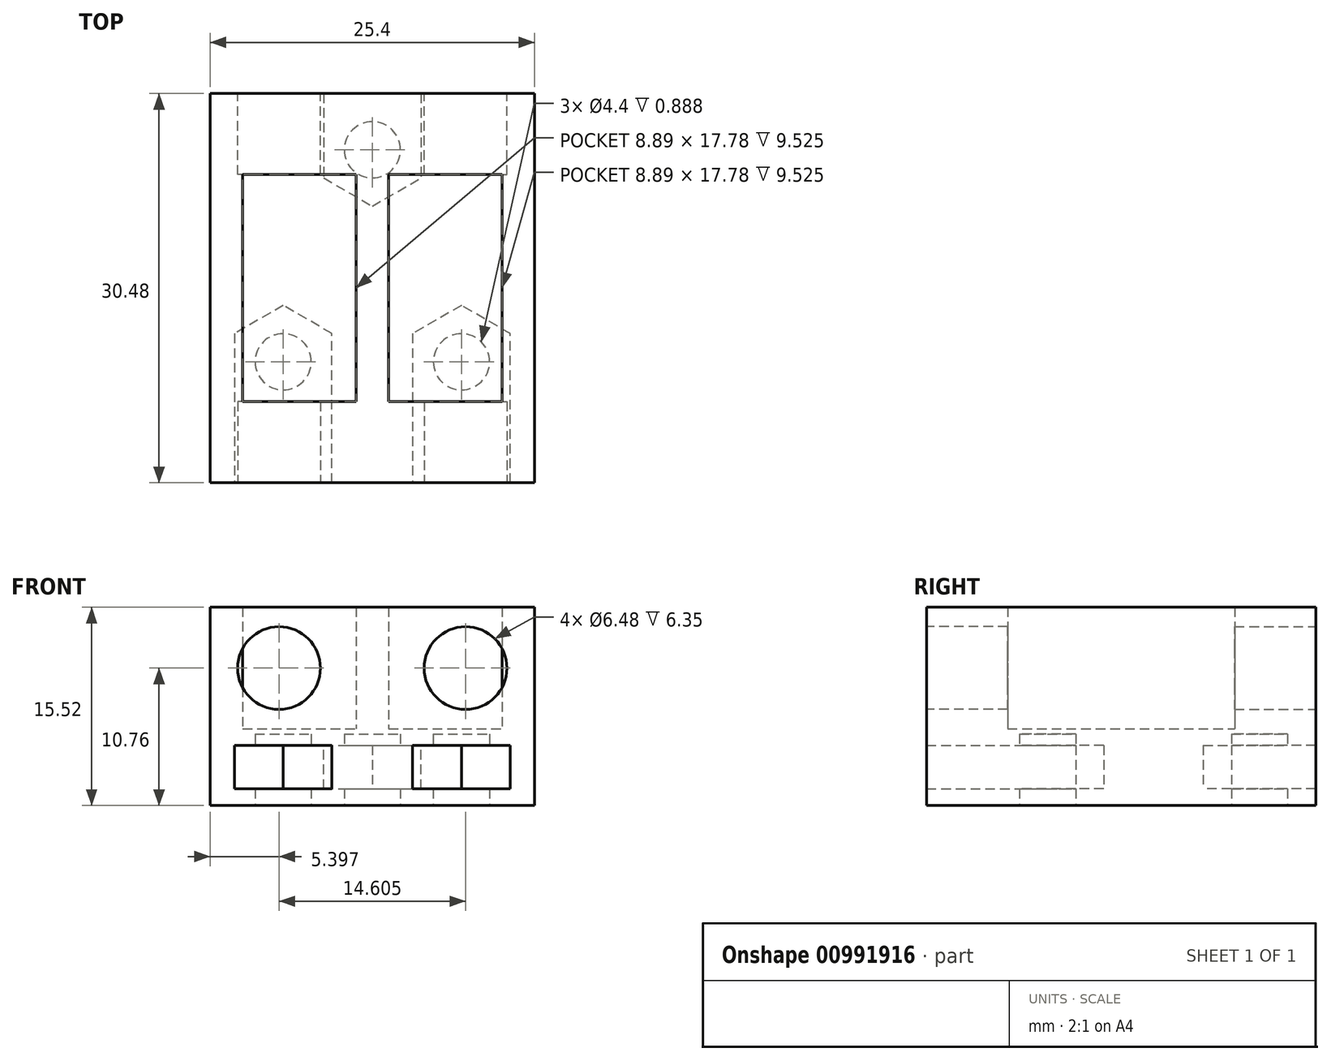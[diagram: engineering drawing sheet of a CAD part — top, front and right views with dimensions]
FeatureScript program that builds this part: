
annotation { "Feature Type Name" : "Feature", "Feature Type Description" : "" }
export const myFeature = defineFeature(function(context is Context, id is Id, definition is map)
    precondition{}
    {
        {
            var Q0;
            Q0=qCreatedBy(makeId("Front.planeOp"),FACE);
            var sketch = newSketch(context, id + "F0", { "sketchPlane" : qUnion([Q0])});
            skLineSegment(sketch, "E0.bottom", {"start": v(12.7, 4.76) * mm, "end": v(-12.7, 4.76) * mm});
            skLineSegment(sketch, "E0.top", {"start": v(12.7, -4.76) * mm, "end": v(-12.7, -4.76) * mm});
            skLineSegment(sketch, "E0.left", {"start": v(12.7, 4.76) * mm, "end": v(12.7, -4.76) * mm});
            skLineSegment(sketch, "E0.right", {"start": v(-12.7, 4.76) * mm, "end": v(-12.7, -4.76) * mm});
            skPoint(sketch, "E0.middle", {"position": v(0, 0) * mm});
            skSolve(sketch);
        }
        {
            var Q0;
            Q0=makeQuery(id+"F0.imprint","IMPRINT",FACE,{"disambiguationData":[TD([[makeQuery(id+"F0.imprint","IMPRINT",EDGE,{"derivedFrom":sQuery(id+"F0.wireOp",EDGE,"E0.bottom")}),1.0]])]});
            extrude(context, id + "F1", {"entities" : qUnion([Q0]), "depth" : 6.35 * mm});
        }
        {
            var Q0;
            Q0=makeQuery(id+"F1.opExtrude","CAP_FACE",FACE,{"disambiguationData":[OSD([sQuery(id+"F0.wireOp",EDGE,"E0.bottom"),sQuery(id+"F0.wireOp",EDGE,"E0.top"),sQuery(id+"F0.wireOp",EDGE,"E0.left"),sQuery(id+"F0.wireOp",EDGE,"E0.right")])],"isStart":false});
            var sketch = newSketch(context, id + "F2", { "sketchPlane" : qUnion([Q0])});
            skLineSegment(sketch, "E1.bottom", {"start": v(-12.7, 4.76) * mm, "end": v(-10.16, 4.76) * mm});
            skLineSegment(sketch, "E1.top", {"start": v(-12.7, -4.76) * mm, "end": v(-10.16, -4.76) * mm});
            skLineSegment(sketch, "E1.left", {"start": v(-12.7, 4.76) * mm, "end": v(-12.7, -4.76) * mm});
            skLineSegment(sketch, "E1.right", {"start": v(-10.16, 4.76) * mm, "end": v(-10.16, -4.76) * mm});
            skLineSegment(sketch, "E2.bottom", {"start": v(1.27, 4.76) * mm, "end": v(-1.27, 4.76) * mm});
            skLineSegment(sketch, "E2.top", {"start": v(1.27, -4.76) * mm, "end": v(-1.27, -4.76) * mm});
            skLineSegment(sketch, "E2.left", {"start": v(1.27, 4.76) * mm, "end": v(1.27, -4.76) * mm});
            skLineSegment(sketch, "E2.right", {"start": v(-1.27, 4.76) * mm, "end": v(-1.27, -4.76) * mm});
            skPoint(sketch, "E2.middle", {"position": v(0, 0) * mm});
            skLineSegment(sketch, "E3", {"start": v(0, 4.76) * mm, "end": v(0, -4.76) * mm, "construction": true});
            skLineSegment(sketch, "E4.MirrorCS", {"start": v(10.16, 4.76) * mm, "end": v(10.16, -4.76) * mm});
            skLineSegment(sketch, "E5.MirrorCS", {"start": v(12.7, 4.76) * mm, "end": v(12.7, -4.76) * mm});
            skLineSegment(sketch, "E6.MirrorCS", {"start": v(12.7, -4.76) * mm, "end": v(10.16, -4.76) * mm});
            skLineSegment(sketch, "E7.MirrorCS", {"start": v(12.7, 4.76) * mm, "end": v(10.16, 4.76) * mm});
            skSolve(sketch);
        }
        {
            var Q0;
            Q0=qSketchRegion(id+"F2",true);
            extrude(context, id + "F3", {"entities" : qUnion([Q0]), "operationType" : NewBodyOperationType.ADD, "depth" : 17.78 * mm});
        }
        {
            var Q0;
            Q0=makeQuery(id+"F3.opExtrude","CAP_FACE",FACE,{"disambiguationData":[OSD([sQuery(id+"F2.wireOp",EDGE,"E1.bottom"),sQuery(id+"F2.wireOp",EDGE,"E1.top"),sQuery(id+"F2.wireOp",EDGE,"E1.left"),sQuery(id+"F2.wireOp",EDGE,"E1.right")])],"isStart":false});
            var sketch = newSketch(context, id + "F4", { "sketchPlane" : qUnion([Q0])});
            skLineSegment(sketch, "E8.bottom", {"start": v(-12.7, 4.76) * mm, "end": v(12.7, 4.76) * mm});
            skLineSegment(sketch, "E8.top", {"start": v(-12.7, -4.76) * mm, "end": v(12.7, -4.76) * mm});
            skLineSegment(sketch, "E8.left", {"start": v(-12.7, 4.76) * mm, "end": v(-12.7, -4.76) * mm});
            skLineSegment(sketch, "E8.right", {"start": v(12.7, 4.76) * mm, "end": v(12.7, -4.76) * mm});
            skSolve(sketch);
        }
        {
            var Q0;
            Q0=qSketchRegion(id+"F4",true);
            extrude(context, id + "F5", {"entities" : qUnion([Q0]), "operationType" : NewBodyOperationType.ADD, "depth" : 6.35 * mm});
        }
        {
            var Q0;
            Q0=makeQuery(id+"F1.opExtrude","CAP_FACE",FACE,{"disambiguationData":[OSD([sQuery(id+"F0.wireOp",EDGE,"E0.bottom"),sQuery(id+"F0.wireOp",EDGE,"E0.top"),sQuery(id+"F0.wireOp",EDGE,"E0.left"),sQuery(id+"F0.wireOp",EDGE,"E0.right")])],"isStart":true});
            var sketch = newSketch(context, id + "F6", { "sketchPlane" : qUnion([Q0])});
            skCircle(sketch, "E9", {"center": v(7.3, 0) * mm, "radius": 3.24 * mm});
            skLineSegment(sketch, "E10", {"start": v(0, 4.76) * mm, "end": v(0, -4.76) * mm, "construction": true});
            skCircle(sketch, "E11.MirrorC", {"center": v(-7.3, 0) * mm, "radius": 3.24 * mm});
            skSolve(sketch);
        }
        {
            var Q0;
            Q0=qSketchRegion(id+"F6",true);
            var Q1;
            {var subQ0=sQuery(id+"F0.wireOp",EDGE,"E0.top");var subQ1=sQuery(id+"F0.wireOp",EDGE,"E0.bottom");Q1=makeQuery(id+"F3.boolean.opBoolean","SPLIT",FACE,{"disambiguationData":[TD([makeQuery(id+"F3.opExtrude","SWEPT_FACE",FACE,{"disambiguationData":[OSD([sQuery(id+"F2.wireOp",EDGE,"E2.left")])]})])],"derivedFrom":makeQuery(id+"F1.opExtrude","CAP_FACE",FACE,{"disambiguationData":[OSD([subQ1,subQ0,sQuery(id+"F0.wireOp",EDGE,"E0.left"),sQuery(id+"F0.wireOp",EDGE,"E0.right")])],"isStart":false})});}
            extrude(context, id + "F7", {"entities" : qUnion([Q0]), "operationType" : NewBodyOperationType.REMOVE, "endBound" : BoundingType.UP_TO_SURFACE, "oppositeDirection" : true, "endBoundEntityFace" : qUnion([Q1]), "depth" : 25.4 * mm});
        }
        {
            var Q0;
            Q0=makeQuery(id+"F5.opExtrude","CAP_FACE",FACE,{"disambiguationData":[OSD([sQuery(id+"F4.wireOp",EDGE,"E8.bottom"),sQuery(id+"F4.wireOp",EDGE,"E8.top"),sQuery(id+"F4.wireOp",EDGE,"E8.left"),sQuery(id+"F4.wireOp",EDGE,"E8.right")])],"isStart":false});
            var sketch = newSketch(context, id + "F8", { "sketchPlane" : qUnion([Q0])});
            skCircle(sketch, "E12", {"center": v(-7.3, 0) * mm, "radius": 3.24 * mm});
            skCircle(sketch, "E13", {"center": v(7.3, 0) * mm, "radius": 3.24 * mm});
            skSolve(sketch);
        }
        {
            var Q0;
            Q0=qSketchRegion(id+"F8",true);
            var Q1;
            {var subQ0=sQuery(id+"F4.wireOp",EDGE,"E8.bottom");var subQ1=sQuery(id+"F4.wireOp",EDGE,"E8.top");Q1=makeQuery(id+"F5.boolean.opBoolean","SPLIT",FACE,{"disambiguationData":[TD([makeQuery(id+"F3.opExtrude","SWEPT_FACE",FACE,{"disambiguationData":[OSD([sQuery(id+"F2.wireOp",EDGE,"E1.right")])]})])],"derivedFrom":makeQuery(id+"F5.opExtrude","CAP_FACE",FACE,{"disambiguationData":[OSD([subQ0,subQ1,sQuery(id+"F4.wireOp",EDGE,"E8.left"),sQuery(id+"F4.wireOp",EDGE,"E8.right")])],"isStart":true})});}
            extrude(context, id + "F9", {"entities" : qUnion([Q0]), "operationType" : NewBodyOperationType.REMOVE, "endBound" : BoundingType.UP_TO_SURFACE, "oppositeDirection" : true, "endBoundEntityFace" : qUnion([Q1]), "depth" : 25.4 * mm});
        }
        {
            var Q0;
            Q0=makeQuery(id+"F5.boolean.opBoolean","MERGE",FACE,{"derivedFrom":[makeQuery(id+"F3.boolean.opBoolean","MERGE",FACE,{"derivedFrom":[makeQuery(id+"F1.opExtrude","SWEPT_FACE",FACE,{"disambiguationData":[OSD([sQuery(id+"F0.wireOp",EDGE,"E0.top")])]}),makeQuery(id+"F3.opExtrude","SWEPT_FACE",FACE,{"disambiguationData":[OSD([sQuery(id+"F2.wireOp",EDGE,"E1.top")])]}),makeQuery(id+"F3.opExtrude","SWEPT_FACE",FACE,{"disambiguationData":[OSD([sQuery(id+"F2.wireOp",EDGE,"E2.top")])]}),makeQuery(id+"F3.opExtrude","SWEPT_FACE",FACE,{"disambiguationData":[OSD([sQuery(id+"F2.wireOp",EDGE,"E6.MirrorCS")])]})]}),makeQuery(id+"F5.opExtrude","SWEPT_FACE",FACE,{"disambiguationData":[OSD([sQuery(id+"F4.wireOp",EDGE,"E8.top")])]})]});
            var sketch = newSketch(context, id + "F10", { "sketchPlane" : qUnion([Q0])});
            skLineSegment(sketch, "E14.bottom", {"start": v(-12.7, 0) * mm, "end": v(12.7, 0) * mm});
            skLineSegment(sketch, "E14.top", {"start": v(-12.7, 30.48) * mm, "end": v(12.7, 30.48) * mm});
            skLineSegment(sketch, "E14.left", {"start": v(-12.7, 30.48) * mm, "end": v(-12.7, 0) * mm});
            skLineSegment(sketch, "E14.right", {"start": v(12.7, 30.48) * mm, "end": v(12.7, 0) * mm});
            skSolve(sketch);
        }
        {
            var Q0;
            Q0=qSketchRegion(id+"F10",true);
            extrude(context, id + "F11", {"entities" : qUnion([Q0]), "operationType" : NewBodyOperationType.ADD, "depth" : 6 * mm});
        }
        {
            var Q0;
            Q0=makeQuery(id+"F11.opExtrude","CAP_FACE",FACE,{"disambiguationData":[OSD([sQuery(id+"F10.wireOp",EDGE,"E14.bottom"),sQuery(id+"F10.wireOp",EDGE,"E14.top"),sQuery(id+"F10.wireOp",EDGE,"E14.left"),sQuery(id+"F10.wireOp",EDGE,"E14.right")])],"isStart":false});
            cPlane(context, id + "F12", {"entities" : qUnion([Q0]), "cplaneType" : CPlaneType.OFFSET, "offset" : 3 * mm, "oppositeDirection" : true, "width" : 152.4 * mm, "height" : 152.4 * mm});
        }
        {
            var Q0;
            Q0=qCreatedBy(id+"F12.planeOp",FACE);
            var sketch = newSketch(context, id + "F13", { "sketchPlane" : qUnion([Q0])});
            skCircle(sketch, "E15.cCircle", {"center": v(0, 4.4) * mm, "radius": 3.82 * mm, "construction": true});
            skLineSegment(sketch, "E15.0", {"start": v(3.82, 6.61) * mm, "end": v(3.82, 2.2) * mm});
            skLineSegment(sketch, "E15.1", {"start": v(3.82, 2.2) * mm, "end": v(0, 0) * mm, "construction": true});
            skLineSegment(sketch, "E15.2", {"start": v(0, 0) * mm, "end": v(-3.82, 2.2) * mm, "construction": true});
            skLineSegment(sketch, "E15.3", {"start": v(-3.82, 2.2) * mm, "end": v(-3.82, 6.61) * mm});
            skLineSegment(sketch, "E15.4", {"start": v(-3.82, 6.61) * mm, "end": v(0, 8.82) * mm});
            skLineSegment(sketch, "E15.5", {"start": v(0, 8.82) * mm, "end": v(3.82, 6.61) * mm});
            skPoint(sketch, "E15.0.midPoint", {"position": v(3.82, 4.4) * mm});
            skCircle(sketch, "E16.cCircle", {"center": v(6.98, 21) * mm, "radius": 3.82 * mm, "construction": true});
            skLineSegment(sketch, "E16.0", {"start": v(10.8, 23.2) * mm, "end": v(10.8, 18.8) * mm});
            skLineSegment(sketch, "E16.1", {"start": v(10.8, 18.8) * mm, "end": v(6.98, 16.6) * mm});
            skLineSegment(sketch, "E16.2", {"start": v(6.98, 16.6) * mm, "end": v(3.16, 18.8) * mm});
            skLineSegment(sketch, "E16.3", {"start": v(3.16, 18.8) * mm, "end": v(3.16, 23.2) * mm});
            skLineSegment(sketch, "E16.4", {"start": v(3.16, 23.2) * mm, "end": v(6.98, 25.41) * mm, "construction": true});
            skLineSegment(sketch, "E16.5", {"start": v(6.98, 25.41) * mm, "end": v(10.8, 23.2) * mm, "construction": true});
            skPoint(sketch, "E16.0.midPoint", {"position": v(10.8, 21) * mm});
            skCircle(sketch, "E17.cCircle", {"center": v(-6.98, 21) * mm, "radius": 3.82 * mm, "construction": true});
            skLineSegment(sketch, "E17.0", {"start": v(-3.16, 23.2) * mm, "end": v(-3.16, 18.8) * mm});
            skLineSegment(sketch, "E17.1", {"start": v(-3.16, 18.8) * mm, "end": v(-6.98, 16.6) * mm});
            skLineSegment(sketch, "E17.2", {"start": v(-6.98, 16.6) * mm, "end": v(-10.8, 18.8) * mm});
            skLineSegment(sketch, "E17.3", {"start": v(-10.8, 18.8) * mm, "end": v(-10.8, 23.2) * mm});
            skLineSegment(sketch, "E17.4", {"start": v(-10.8, 23.2) * mm, "end": v(-6.98, 25.41) * mm, "construction": true});
            skLineSegment(sketch, "E17.5", {"start": v(-6.98, 25.41) * mm, "end": v(-3.16, 23.2) * mm, "construction": true});
            skPoint(sketch, "E17.0.midPoint", {"position": v(-3.16, 21) * mm});
            skLineSegment(sketch, "E18", {"start": v(-10.8, 23.2) * mm, "end": v(-10.8, 30.48) * mm});
            skLineSegment(sketch, "E19", {"start": v(-10.8, 30.48) * mm, "end": v(-3.16, 30.48) * mm});
            skLineSegment(sketch, "E20", {"start": v(-3.16, 30.48) * mm, "end": v(-3.16, 23.2) * mm});
            skLineSegment(sketch, "E21", {"start": v(3.16, 23.2) * mm, "end": v(3.16, 30.48) * mm});
            skLineSegment(sketch, "E22", {"start": v(3.16, 30.48) * mm, "end": v(10.8, 30.48) * mm});
            skLineSegment(sketch, "E23", {"start": v(10.8, 30.48) * mm, "end": v(10.8, 23.2) * mm});
            skLineSegment(sketch, "E24", {"start": v(-3.82, 2.2) * mm, "end": v(-3.82, -0.01) * mm});
            skLineSegment(sketch, "E25", {"start": v(-3.82, -0.01) * mm, "end": v(3.82, -0.01) * mm});
            skLineSegment(sketch, "E26", {"start": v(3.82, -0.01) * mm, "end": v(3.82, 2.2) * mm});
            skSolve(sketch);
        }
        {
            var Q0;
            Q0=makeQuery(id+"F13.imprint","IMPRINT",FACE,{"disambiguationData":[TD([[makeQuery(id+"F13.imprint","IMPRINT",EDGE,{"derivedFrom":sQuery(id+"F13.wireOp",EDGE,"E17.0")}),-1.0]])]});
            var Q1;
            Q1=makeQuery(id+"F13.imprint","IMPRINT",FACE,{"disambiguationData":[TD([[makeQuery(id+"F13.imprint","IMPRINT",EDGE,{"derivedFrom":sQuery(id+"F13.wireOp",EDGE,"E16.0")}),-1.0]])]});
            var Q2;
            Q2=makeQuery(id+"F13.imprint","IMPRINT",FACE,{"disambiguationData":[TD([[makeQuery(id+"F13.imprint","IMPRINT",EDGE,{"derivedFrom":sQuery(id+"F13.wireOp",EDGE,"E15.0")}),-1.0]])]});
            extrude(context, id + "F14", {"entities" : qUnion([Q0, Q1, Q2]), "operationType" : NewBodyOperationType.REMOVE, "oppositeDirection" : true, "depth" : 3.4 / 2 * mm, "hasSecondDirection" : true, "secondDirectionOppositeDirection" : false, "secondDirectionDepth" : 3.4 / 2 * mm});
        }
        {
            var Q0;
            Q0=makeQuery(id+"F11.opExtrude","CAP_FACE",FACE,{"disambiguationData":[OSD([sQuery(id+"F10.wireOp",EDGE,"E14.bottom"),sQuery(id+"F10.wireOp",EDGE,"E14.top"),sQuery(id+"F10.wireOp",EDGE,"E14.left"),sQuery(id+"F10.wireOp",EDGE,"E14.right")])],"isStart":false});
            var sketch = newSketch(context, id + "F15", { "sketchPlane" : qUnion([Q0])});
            skCircle(sketch, "E27", {"center": v(0, 4.4) * mm, "radius": 2.2 * mm});
            skCircle(sketch, "E28", {"center": v(6.98, 21) * mm, "radius": 2.2 * mm});
            skCircle(sketch, "E29", {"center": v(-6.98, 21) * mm, "radius": 2.2 * mm});
            skSolve(sketch);
        }
        {
            var Q0;
            Q0=qSketchRegion(id+"F15",true);
            extrude(context, id + "F16", {"entities" : qUnion([Q0]), "operationType" : NewBodyOperationType.REMOVE, "oppositeDirection" : true, "depth" : 5.6 * mm});
        }
    });
